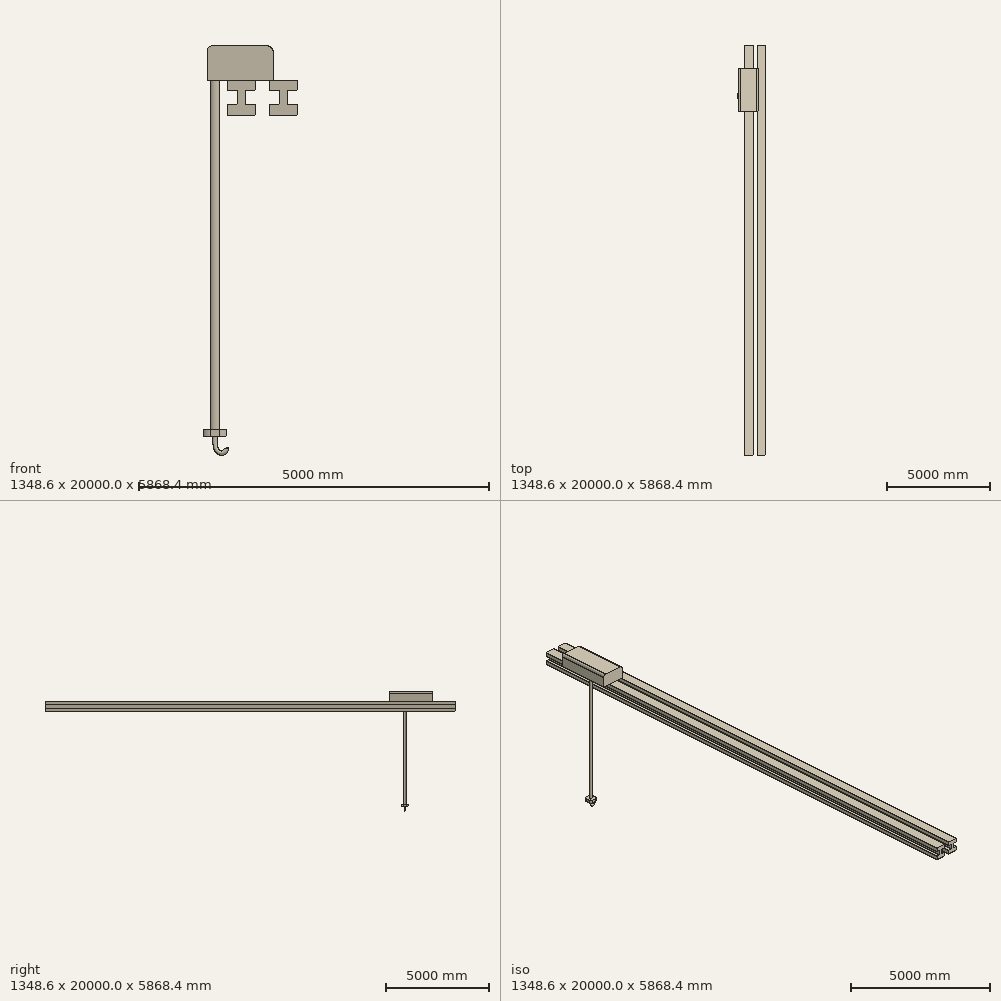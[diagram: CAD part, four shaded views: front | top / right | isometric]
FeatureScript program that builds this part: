
annotation { "Feature Type Name" : "Feature", "Feature Type Description" : "" }
export const myFeature = defineFeature(function(context is Context, id is Id, definition is map)
    precondition{}
    {
        {
            var Q0;
            Q0=qCreatedBy(makeId("Front.planeOp"),FACE);
            var sketch = newSketch(context, id + "F0", { "sketchPlane" : qUnion([Q0])});
            skLineSegment(sketch, "E0", {"start": v(-193.95, 98.01) * mm, "end": v(-193.95, 248.01) * mm});
            skLineSegment(sketch, "E1", {"start": v(-193.95, 248.01) * mm, "end": v(206.05, 248.01) * mm});
            skLineSegment(sketch, "E2", {"start": v(206.05, 248.01) * mm, "end": v(206.05, 98.01) * mm});
            skLineSegment(sketch, "E3", {"start": v(206.05, 98.01) * mm, "end": v(62.97, 98.01) * mm});
            skLineSegment(sketch, "E4", {"start": v(62.97, 98.01) * mm, "end": v(62.97, -101.99) * mm});
            skLineSegment(sketch, "E5", {"start": v(62.97, -101.99) * mm, "end": v(206.05, -101.99) * mm});
            skLineSegment(sketch, "E6", {"start": v(206.05, -101.99) * mm, "end": v(206.05, -251.99) * mm});
            skLineSegment(sketch, "E7", {"start": v(206.05, -251.99) * mm, "end": v(-193.95, -251.99) * mm});
            skLineSegment(sketch, "E8", {"start": v(-193.95, -251.99) * mm, "end": v(-193.95, -101.99) * mm});
            skLineSegment(sketch, "E9", {"start": v(-193.95, -101.99) * mm, "end": v(-50.88, -101.99) * mm});
            skLineSegment(sketch, "E10", {"start": v(-50.88, -101.99) * mm, "end": v(-50.88, 98.01) * mm});
            skLineSegment(sketch, "E11", {"start": v(-50.88, 98.01) * mm, "end": v(-193.95, 98.01) * mm});
            skLineSegment(sketch, "E12.1.0.0", {"start": v(406.05, 98.01) * mm, "end": v(406.05, 248.01) * mm});
            skLineSegment(sketch, "E12.1.0.1", {"start": v(406.05, 248.01) * mm, "end": v(806.05, 248.01) * mm});
            skLineSegment(sketch, "E12.1.0.2", {"start": v(806.05, 248.01) * mm, "end": v(806.05, 98.01) * mm});
            skLineSegment(sketch, "E12.1.0.3", {"start": v(806.05, 98.01) * mm, "end": v(662.97, 98.01) * mm});
            skLineSegment(sketch, "E12.1.0.4", {"start": v(662.97, 98.01) * mm, "end": v(662.97, -101.99) * mm});
            skLineSegment(sketch, "E12.1.0.5", {"start": v(662.97, -101.99) * mm, "end": v(806.05, -101.99) * mm});
            skLineSegment(sketch, "E12.1.0.6", {"start": v(806.05, -101.99) * mm, "end": v(806.05, -251.99) * mm});
            skLineSegment(sketch, "E12.1.0.7", {"start": v(806.05, -251.99) * mm, "end": v(406.05, -251.99) * mm});
            skLineSegment(sketch, "E12.1.0.8", {"start": v(406.05, -251.99) * mm, "end": v(406.05, -101.99) * mm});
            skLineSegment(sketch, "E12.1.0.9", {"start": v(406.05, -101.99) * mm, "end": v(549.12, -101.99) * mm});
            skLineSegment(sketch, "E12.1.0.10", {"start": v(549.12, -101.99) * mm, "end": v(549.12, 98.01) * mm});
            skLineSegment(sketch, "E12.1.0.11", {"start": v(549.12, 98.01) * mm, "end": v(406.05, 98.01) * mm});
            skLineSegment(sketch, "E12.direction1", {"start": v(-193.95, -251.99) * mm, "end": v(406.05, -251.99) * mm, "construction": true});
            skSolve(sketch);
        }
        {
            var Q0;
            Q0 = qSketchRegion(id + "F0", true);
            extrude(context, id + "F1", {"entities" : qUnion([Q0]), "depth" : 20000 * mm, "offsetDistance" : 25 * mm});
        }
        {
            var Q0;
            Q0=makeQuery(id+"F1.opExtrude","SWEPT_FACE",FACE,{"disambiguationData":[OSD([sQuery(id+"F0.wireOp",EDGE,"E1")])]});
            var sketch = newSketch(context, id + "F2", { "sketchPlane" : qUnion([Q0])});
            skLineSegment(sketch, "E13.bottom", {"start": v(-490.54, -1101.95) * mm, "end": v(457.37, -1101.95) * mm});
            skLineSegment(sketch, "E13.top", {"start": v(-490.54, -3229) * mm, "end": v(457.37, -3229) * mm});
            skLineSegment(sketch, "E13.left", {"start": v(-490.54, -1101.95) * mm, "end": v(-490.54, -3229) * mm});
            skLineSegment(sketch, "E13.right", {"start": v(457.37, -1101.95) * mm, "end": v(457.37, -3229) * mm});
            skSolve(sketch);
        }
        {
            var Q0;
            Q0 = qSketchRegion(id + "F2", true);
            extrude(context, id + "F3", {"entities" : qUnion([Q0]), "depth" : 500 * mm, "offsetDistance" : 25 * mm});
        }
        {
            var Q0;
            Q0=makeQuery(id+"F3.opExtrude","CAP_EDGE",EDGE,{"disambiguationData":[OSD([sQuery(id+"F2.wireOp",EDGE,"E13.right")])],"isStart":false});
            var Q1;
            Q1=makeQuery(id+"F3.opExtrude","CAP_EDGE",EDGE,{"disambiguationData":[OSD([sQuery(id+"F2.wireOp",EDGE,"E13.left")])],"isStart":false});
            fillet(context, id + "F4", {"entities" : qUnion([Q0, Q1]), "radius" : 100 * mm, "tangentPropagation" : true, "allowEdgeOverflow" : false});
        }
        {
            var Q0;
            Q0=makeQuery(id+"F3.opExtrude","CAP_EDGE",EDGE,{"disambiguationData":[OSD([sQuery(id+"F2.wireOp",EDGE,"E13.left")])],"isStart":true});
            var Q1;
            Q1=makeQuery(id+"F3.opExtrude","CAP_EDGE",EDGE,{"disambiguationData":[OSD([sQuery(id+"F2.wireOp",EDGE,"E13.right")])],"isStart":true});
            fillet(context, id + "F5", {"entities" : qUnion([Q0, Q1]), "radius" : 5 * mm, "tangentPropagation" : true, "allowEdgeOverflow" : false});
        }
        {
            var Q0;
            Q0=makeQuery(id+"F3.opExtrude","CAP_FACE",FACE,{"disambiguationData":[OSD([sQuery(id+"F2.wireOp",EDGE,"E13.bottom"),sQuery(id+"F2.wireOp",EDGE,"E13.top"),sQuery(id+"F2.wireOp",EDGE,"E13.left"),sQuery(id+"F2.wireOp",EDGE,"E13.right")])],"isStart":true});
            var sketch = newSketch(context, id + "F6", { "sketchPlane" : qUnion([Q0])});
            skCircle(sketch, "E14", {"center": v(-374.4, 2459.18) * mm, "radius": 68.15 * mm});
            skSolve(sketch);
        }
        {
            var Q0;
            Q0 = qSketchRegion(id + "F6", true);
            extrude(context, id + "F7", {"entities" : qUnion([Q0]), "depth" : 5000 * mm, "offsetDistance" : 25 * mm});
        }
        {
            var Q0;
            Q0=makeQuery(id+"F7.opExtrude","CAP_FACE",FACE,{"disambiguationData":[OSD([sQuery(id+"F6.wireOp",EDGE,"E14")])],"isStart":false});
            var sketch = newSketch(context, id + "F8", { "sketchPlane" : qUnion([Q0])});
            skLineSegment(sketch, "E15.bottom", {"start": v(-542.56, 2627.33) * mm, "end": v(-206.26, 2627.33) * mm});
            skLineSegment(sketch, "E15.top", {"start": v(-542.56, 2291.03) * mm, "end": v(-206.26, 2291.03) * mm});
            skLineSegment(sketch, "E15.left", {"start": v(-542.56, 2627.33) * mm, "end": v(-542.56, 2291.03) * mm});
            skLineSegment(sketch, "E15.right", {"start": v(-206.26, 2627.33) * mm, "end": v(-206.26, 2291.03) * mm});
            skSolve(sketch);
        }
        {
            var Q0;
            Q0 = qSketchRegion(id + "F8", true);
            extrude(context, id + "F9", {"entities" : qUnion([Q0]), "depth" : 100 * mm, "offsetDistance" : 25 * mm});
        }
        {
            var Q0;
            Q0=makeQuery(id+"F9.opExtrude","CAP_FACE",FACE,{"disambiguationData":[OSD([sQuery(id+"F8.wireOp",EDGE,"E15.bottom"),sQuery(id+"F8.wireOp",EDGE,"E15.top"),sQuery(id+"F8.wireOp",EDGE,"E15.left"),sQuery(id+"F8.wireOp",EDGE,"E15.right")])],"isStart":false});
            var sketch = newSketch(context, id + "F10", { "sketchPlane" : qUnion([Q0])});
            skCircle(sketch, "E16", {"center": v(-374.4, 2459.18) * mm, "radius": 31.43 * mm});
            skLineSegment(sketch, "E17", {"start": v(-542.56, 2459.18) * mm, "end": v(-206.26, 2459.18) * mm});
            skSolve(sketch);
        }
        {
            var Q0;
            Q0=makeQuery(id+"F9.opExtrude","SWEPT_FACE",FACE,{"disambiguationData":[OSD([sQuery(id+"F8.wireOp",EDGE,"E15.bottom")])]});
            var Q1;
            Q1=makeQuery(id+"F9.opExtrude","SWEPT_FACE",FACE,{"disambiguationData":[OSD([sQuery(id+"F8.wireOp",EDGE,"E15.top")])]});
            cPlane(context, id + "F11", {"entities" : qUnion([Q0, Q1]), "cplaneType" : CPlaneType.MID_PLANE, "offset" : 25 * mm, "width" : 150 * mm, "height" : 150 * mm});
        }
        {
            var Q0;
            Q0=qCreatedBy(id+"F11.planeOp",FACE);
            var sketch = newSketch(context, id + "F12", { "sketchPlane" : qUnion([Q0])});
            skFitSpline(sketch, "E18", {"points": [v(-374.64, -4852.24) * mm, v(-375.43, -4941.06) * mm, v(-354.64, -5036.78) * mm, v(-311.01, -5080.4) * mm, v(-255.49, -5085.7) * mm, v(-214.5, -5046.03) * mm, v(-211.86, -5011.66) * mm], "startDerivative": vector(-20.82, -437.8) * mm, "endDerivative": vector(-27.87, 273.1) * mm});
            skSolve(sketch);
        }
        {
            var Q0;
            Q0 = qSketchRegion(id + "F10", true);
            var Q1;
            Q1 = qConstructionFilter(qBodyType(qCreatedBy(id + "F12" ,EDGE), BodyType.WIRE), ConstructionObject.NO);
            sweep(context, id + "F13", {"profiles" : qUnion([Q0]), "path" : qUnion([Q1])});
        }
        {
            var Q0;
            Q0=makeQuery(id+"F9.opExtrude","SWEPT_EDGE",EDGE,{"disambiguationData":[OSD([sQuery(id+"F8.wireOp",EDGE,"E15.top"),sQuery(id+"F8.wireOp",EDGE,"E15.right")])]});
            var Q1;
            Q1=makeQuery(id+"F9.opExtrude","SWEPT_EDGE",EDGE,{"disambiguationData":[OSD([sQuery(id+"F8.wireOp",EDGE,"E15.top"),sQuery(id+"F8.wireOp",EDGE,"E15.left")])]});
            var Q2;
            Q2=makeQuery(id+"F9.opExtrude","SWEPT_EDGE",EDGE,{"disambiguationData":[OSD([sQuery(id+"F8.wireOp",EDGE,"E15.bottom"),sQuery(id+"F8.wireOp",EDGE,"E15.right")])]});
            var Q3;
            Q3=makeQuery(id+"F9.opExtrude","SWEPT_EDGE",EDGE,{"disambiguationData":[OSD([sQuery(id+"F8.wireOp",EDGE,"E15.bottom"),sQuery(id+"F8.wireOp",EDGE,"E15.left")])]});
            fillet(context, id + "F14", {"entities" : qUnion([Q0, Q1, Q2, Q3]), "radius" : 100 * mm, "tangentPropagation" : true, "allowEdgeOverflow" : false});
        }
        {
            var Q0;
            Q0=makeQuery(id+"F13.opSweep","CAP_EDGE",EDGE,{"disambiguationData":[OSD([sQuery(id+"F10.wireOp",EDGE,"E16"),sQuery(id+"F12.wireOp",VERTEX,"E18.end")])],"isStart":false});
            chamfer(context, id + "F15", {"entities" : qUnion([Q0]), "width" : 10 * mm, "tangentPropagation" : true});
        }
    });
